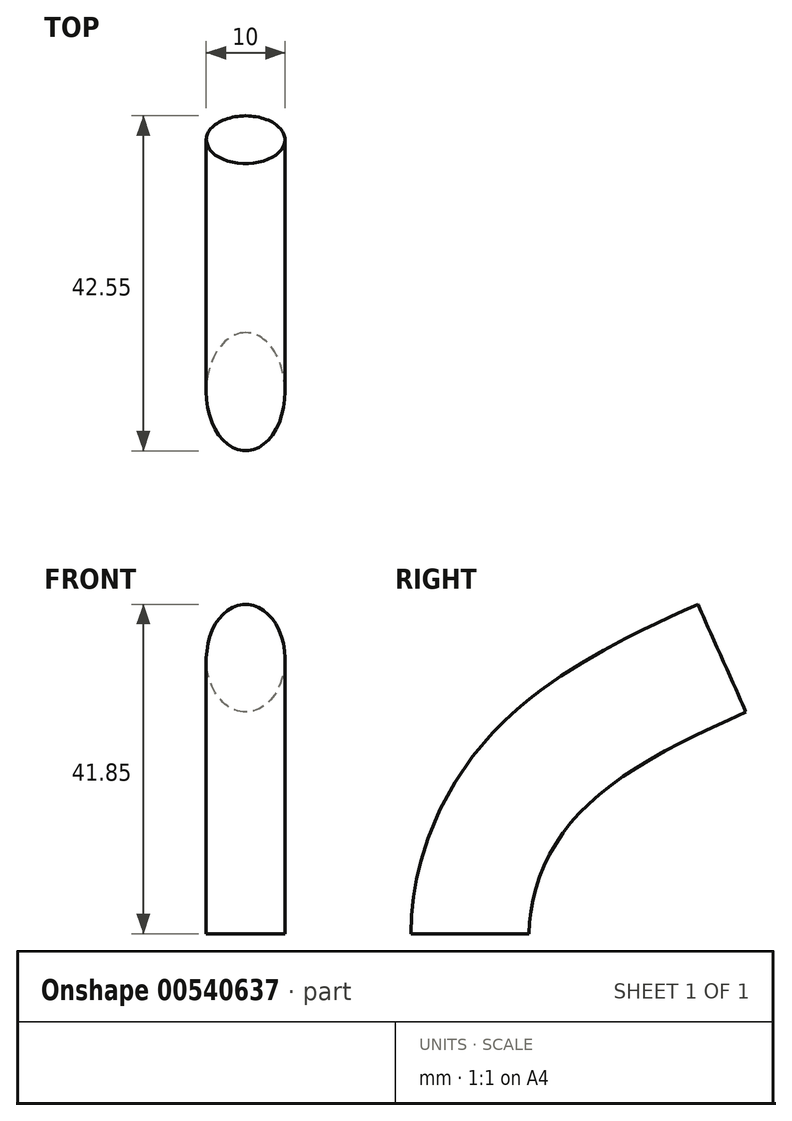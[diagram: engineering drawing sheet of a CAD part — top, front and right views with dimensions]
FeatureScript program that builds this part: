
annotation { "Feature Type Name" : "Feature", "Feature Type Description" : "" }
export const myFeature = defineFeature(function(context is Context, id is Id, definition is map)
    precondition{}
    {
        {
            var Q0;
            Q0=qCreatedBy(makeId("Right.planeOp"),FACE);
            var sketch = newSketch(context, id + "F0", { "sketchPlane" : qUnion([Q0])});
            skFitSpline(sketch, "E0", {"points": [v(0, 0) * mm, v(8, 20) * mm, v(32, 35) * mm], "startDerivative": vector(0, 45.07) * mm, "endDerivative": vector(50.56, 22.47) * mm});
            skSolve(sketch);
        }
        {
            var Q0;
            Q0=qCreatedBy(makeId("Top.planeOp"),FACE);
            var sketch = newSketch(context, id + "F1", { "sketchPlane" : qUnion([Q0])});
            skEllipse(sketch, "E1", {"center": v(0, 0) * mm, "majorRadius": 7.5 * mm, "minorRadius": 5 * mm, "majorAxis": v(0, 1)});
            skSolve(sketch);
        }
        {
            var Q0;
            Q0=makeQuery(id+"F1.imprint","IMPRINT",FACE,{"disambiguationData":[TD([[makeQuery(id+"F1.imprint","IMPRINT",EDGE,{"derivedFrom":sQuery(id+"F1.wireOp",EDGE,"E1")}),1.0]])]});
            var Q1;
            Q1=sQuery(id+"F0.wireOp",EDGE,"E0");
            sweep(context, id + "F2", {"profiles" : qUnion([Q0]), "path" : qUnion([Q1])});
        }
    });
